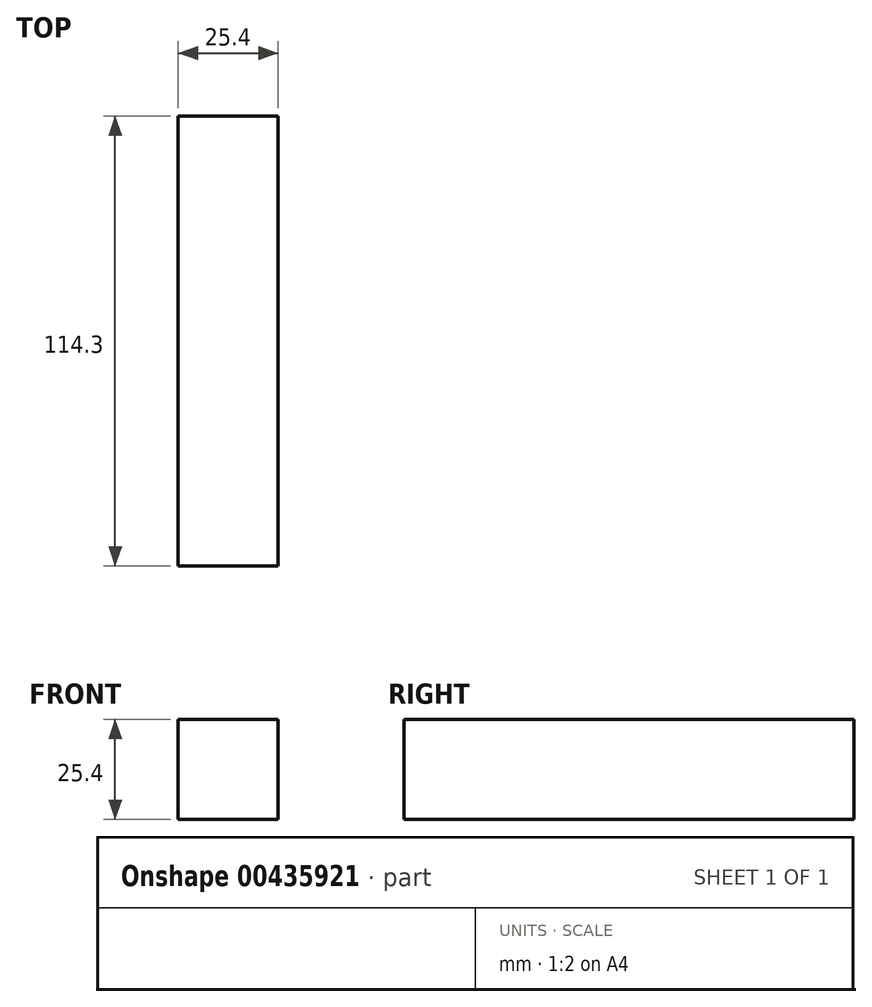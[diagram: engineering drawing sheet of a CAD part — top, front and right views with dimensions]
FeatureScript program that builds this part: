
annotation { "Feature Type Name" : "Feature", "Feature Type Description" : "" }
export const myFeature = defineFeature(function(context is Context, id is Id, definition is map)
    precondition{}
    {
        {
            var Q0;
            Q0=qCreatedBy(makeId("Front.planeOp"),FACE);
            var sketch = newSketch(context, id + "F0", { "sketchPlane" : qUnion([Q0])});
            skLineSegment(sketch, "E0.bottom", {"start": v(-12.7, 12.7) * mm, "end": v(12.7, 12.7) * mm});
            skLineSegment(sketch, "E0.top", {"start": v(-12.7, -12.7) * mm, "end": v(12.7, -12.7) * mm});
            skLineSegment(sketch, "E0.left", {"start": v(-12.7, 12.7) * mm, "end": v(-12.7, -12.7) * mm});
            skLineSegment(sketch, "E0.right", {"start": v(12.7, 12.7) * mm, "end": v(12.7, -12.7) * mm});
            skPoint(sketch, "E0.middle", {"position": v(0, 0) * mm});
            skSolve(sketch);
        }
        {
            var Q0;
            Q0=makeQuery(id+"F0.imprint","IMPRINT",FACE,{"disambiguationData":[TD([[makeQuery(id+"F0.imprint","IMPRINT",EDGE,{"derivedFrom":sQuery(id+"F0.wireOp",EDGE,"E0.bottom")}),-1.0]])]});
            extrude(context, id + "F1", {"entities" : qUnion([Q0]), "depth" : 114.3 * mm});
        }
    });
